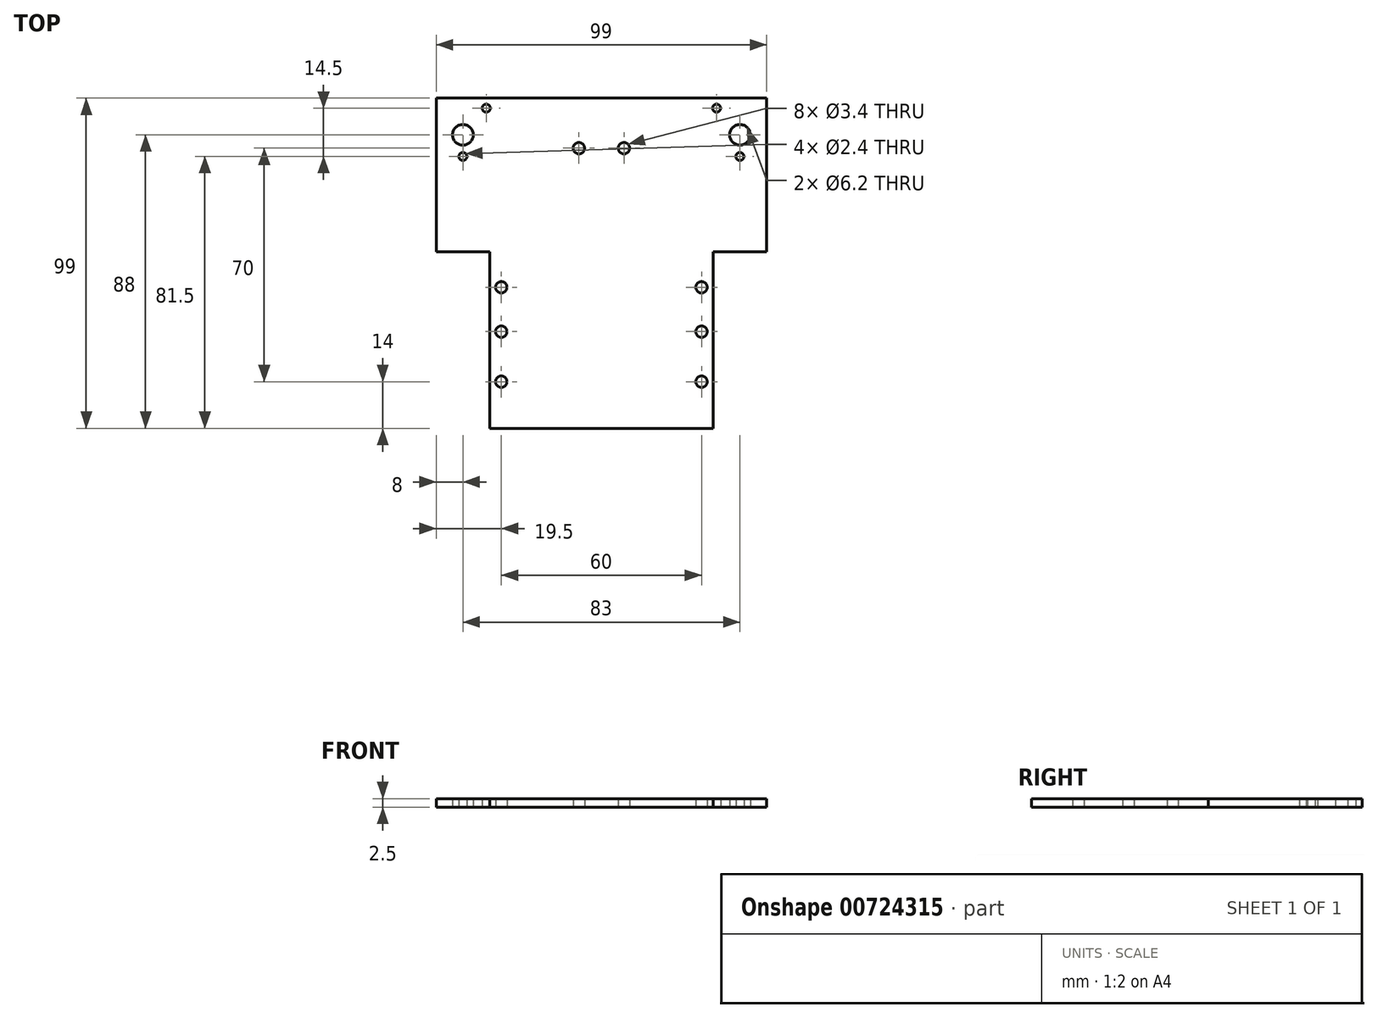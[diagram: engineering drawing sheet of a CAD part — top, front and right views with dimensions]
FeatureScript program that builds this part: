
annotation { "Feature Type Name" : "Feature", "Feature Type Description" : "" }
export const myFeature = defineFeature(function(context is Context, id is Id, definition is map)
    precondition{}
    {
        {
            var Q0;
            Q0=qCreatedBy(makeId("Top.planeOp"),FACE);
            var sketch = newSketch(context, id + "F0", { "sketchPlane" : qUnion([Q0])});
            skLineSegment(sketch, "E0", {"start": v(0, 49) * mm, "end": v(-49.5, 49) * mm});
            skLineSegment(sketch, "E1", {"start": v(-49.5, 49) * mm, "end": v(-49.5, 3) * mm});
            skLineSegment(sketch, "E2", {"start": v(-49.5, 3) * mm, "end": v(-33.5, 3) * mm});
            skLineSegment(sketch, "E3", {"start": v(-33.5, 3) * mm, "end": v(-33.5, -50) * mm});
            skLineSegment(sketch, "E4", {"start": v(-33.5, -50) * mm, "end": v(0, -50) * mm});
            skCircle(sketch, "E5", {"center": v(-41.5, 38) * mm, "radius": 3.1 * mm});
            skCircle(sketch, "E6", {"center": v(-41.5, 31.5) * mm, "radius": 1.2 * mm});
            skCircle(sketch, "E7", {"center": v(-34.5, 46) * mm, "radius": 1.2 * mm});
            skCircle(sketch, "E8", {"center": v(-6.75, 34) * mm, "radius": 1.7 * mm});
            skCircle(sketch, "E9", {"center": v(-30, -7.7) * mm, "radius": 1.7 * mm});
            skCircle(sketch, "E10", {"center": v(-30, -21) * mm, "radius": 1.7 * mm});
            skCircle(sketch, "E11", {"center": v(-30, -36) * mm, "radius": 1.7 * mm});
            skCircle(sketch, "E12.MirrorC", {"center": v(30, -36) * mm, "radius": 1.7 * mm});
            skCircle(sketch, "E13.MirrorC", {"center": v(30, -21) * mm, "radius": 1.7 * mm});
            skCircle(sketch, "E14.MirrorC", {"center": v(30, -7.7) * mm, "radius": 1.7 * mm});
            skCircle(sketch, "E15.MirrorC", {"center": v(6.75, 34) * mm, "radius": 1.7 * mm});
            skCircle(sketch, "E16.MirrorC", {"center": v(34.5, 46) * mm, "radius": 1.2 * mm});
            skCircle(sketch, "E17.MirrorC", {"center": v(41.5, 31.5) * mm, "radius": 1.2 * mm});
            skCircle(sketch, "E18.MirrorC", {"center": v(41.5, 38) * mm, "radius": 3.1 * mm});
            skLineSegment(sketch, "E19.MirrorCS", {"start": v(33.5, -50) * mm, "end": v(0, -50) * mm});
            skLineSegment(sketch, "E20.MirrorCS", {"start": v(33.5, 3) * mm, "end": v(33.5, -50) * mm});
            skLineSegment(sketch, "E21.MirrorCS", {"start": v(49.5, 3) * mm, "end": v(33.5, 3) * mm});
            skLineSegment(sketch, "E22.MirrorCS", {"start": v(0, 49) * mm, "end": v(49.5, 49) * mm});
            skLineSegment(sketch, "E23.MirrorCS", {"start": v(49.5, 49) * mm, "end": v(49.5, 3) * mm});
            skLineSegment(sketch, "E24", {"start": v(-30, -7.7) * mm, "end": v(-30, -50) * mm, "construction": true});
            skSolve(sketch);
        }
        {
            var Q0;
            Q0 = qSketchRegion(id + "F0", true);
            extrude(context, id + "F1", {"entities" : qUnion([Q0]), "depth" : 2.5 * mm, "offsetDistance" : 25 * mm});
        }
    });
